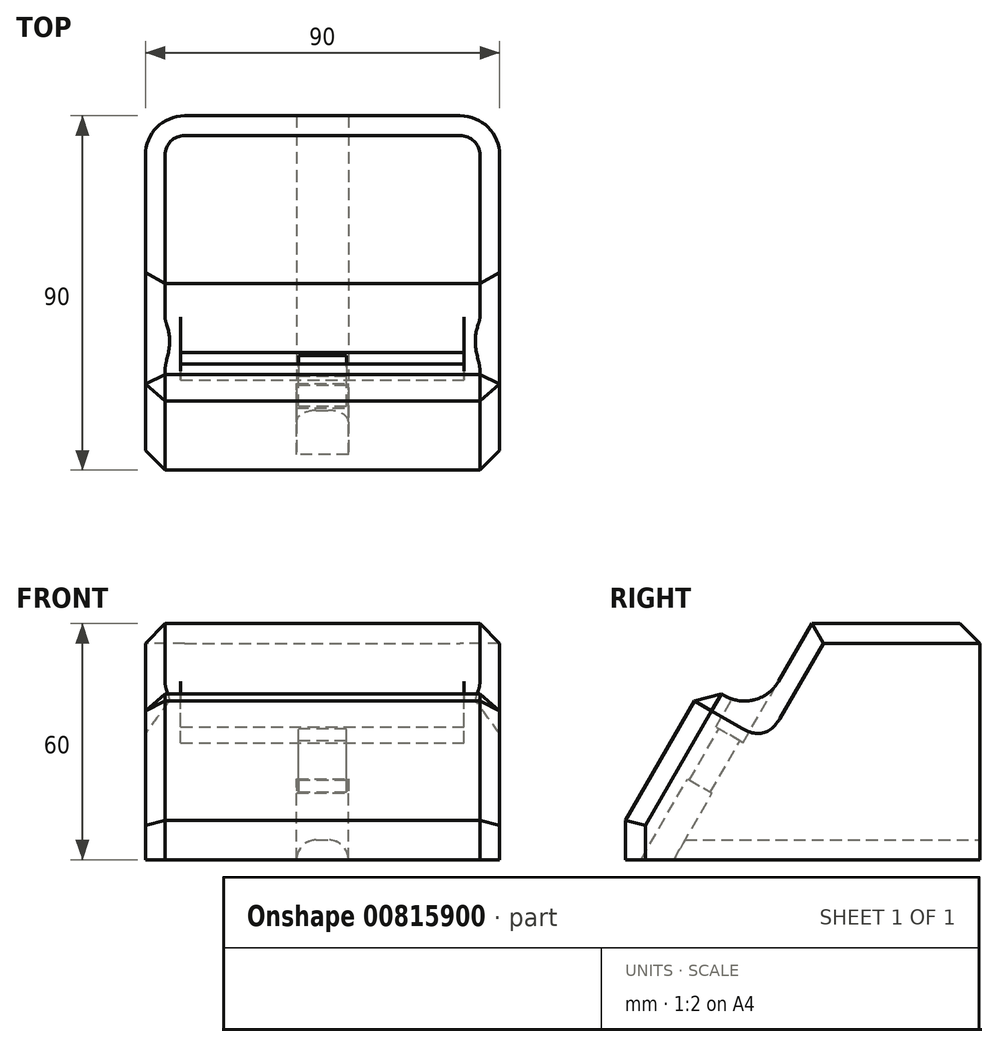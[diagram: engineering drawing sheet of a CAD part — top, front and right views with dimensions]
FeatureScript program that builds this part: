
annotation { "Feature Type Name" : "Feature", "Feature Type Description" : "" }
export const myFeature = defineFeature(function(context is Context, id is Id, definition is map)
    precondition{}
    {
        {
            var Q0;
            Q0=qCreatedBy(makeId("Top.planeOp"),FACE);
            var sketch = newSketch(context, id + "F0", { "sketchPlane" : qUnion([Q0])});
            skLineSegment(sketch, "E0.bottom", {"start": v(45, -45) * mm, "end": v(-45, -45) * mm});
            skLineSegment(sketch, "E0.top", {"start": v(35, 45) * mm, "end": v(-35, 45) * mm});
            skLineSegment(sketch, "E0.left", {"start": v(45, -45) * mm, "end": v(45, 35) * mm});
            skLineSegment(sketch, "E0.right", {"start": v(-45, -45) * mm, "end": v(-45, 35) * mm});
            skPoint(sketch, "E0.middle", {"position": v(0, 0) * mm});
            skPoint(sketch, "E1.visualSharp", {"position": v(-45, 45) * mm});
            skArc(sketch, "E1.filletArc", {"start": v(-35, 45) * mm, "mid": v(-42.07, 42.07) * mm, "end": v(-45, 35) * mm});
            skPoint(sketch, "E2.visualSharp", {"position": v(45, 45) * mm});
            skArc(sketch, "E2.filletArc", {"start": v(45, 35) * mm, "mid": v(42.07, 42.07) * mm, "end": v(35, 45) * mm});
            skSolve(sketch);
        }
        {
            var Q0;
            Q0=makeQuery(id+"F0.imprint","IMPRINT",FACE,{"disambiguationData":[TD([[makeQuery(id+"F0.imprint","IMPRINT",EDGE,{"derivedFrom":sQuery(id+"F0.wireOp",EDGE,"E0.bottom")}),-1.0]])]});
            extrude(context, id + "F1", {"entities" : qUnion([Q0]), "depth" : 60 * mm, "offsetDistance" : 25 * mm});
        }
        {
            var Q0;
            Q0=qCreatedBy(makeId("Right.planeOp"),FACE);
            var sketch = newSketch(context, id + "F2", { "sketchPlane" : qUnion([Q0])});
            skLineSegment(sketch, "E3", {"start": v(-45, 10) * mm, "end": v(-25, 44.64) * mm});
            skLineSegment(sketch, "E4", {"start": v(-45, 60) * mm, "end": v(2.34, 60) * mm});
            skLineSegment(sketch, "E5", {"start": v(-45, 60) * mm, "end": v(-45, 10) * mm});
            skLineSegment(sketch, "E6", {"start": v(-25, 44.64) * mm, "end": v(-11.14, 36.64) * mm});
            skLineSegment(sketch, "E7", {"start": v(-11.14, 36.64) * mm, "end": v(2.34, 60) * mm});
            skSolve(sketch);
        }
        {
            var Q0;
            Q0 = qSketchRegion(id + "F2", true);
            extrude(context, id + "F3", {"entities" : qUnion([Q0]), "operationType" : NewBodyOperationType.REMOVE, "endBound" : BoundingType.THROUGH_ALL, "oppositeDirection" : true, "depth" : 25 * mm, "offsetDistance" : 25 * mm, "hasSecondDirection" : true, "secondDirectionBound" : SecondDirectionBoundingType.THROUGH_ALL, "secondDirectionOppositeDirection" : false, "secondDirectionDepth" : 25 * mm});
        }
        {
            var Q0;
            Q0=makeQuery(id+"F3.boolean.opBoolean","COPY",FACE,{"derivedFrom":makeQuery(id+"F3.opExtrude","SWEPT_FACE",FACE,{"disambiguationData":[OSD([sQuery(id+"F2.wireOp",EDGE,"E6")])]})});
            var sketch = newSketch(context, id + "F4", { "sketchPlane" : qUnion([Q0])});
            skLineSegment(sketch, "E8.bottom", {"start": v(-36, -27.97) * mm, "end": v(36, -27.97) * mm});
            skLineSegment(sketch, "E8.top", {"start": v(-36, -35.97) * mm, "end": v(36, -35.97) * mm});
            skLineSegment(sketch, "E8.left", {"start": v(-36, -27.97) * mm, "end": v(-36, -35.97) * mm});
            skLineSegment(sketch, "E8.right", {"start": v(36, -27.97) * mm, "end": v(36, -35.97) * mm});
            skLineSegment(sketch, "E9", {"start": v(0, 0) * mm, "end": v(0, -27.97) * mm, "construction": true});
            skSolve(sketch);
        }
        {
            var Q0;
            Q0 = qSketchRegion(id + "F4", true);
            extrude(context, id + "F5", {"entities" : qUnion([Q0]), "operationType" : NewBodyOperationType.REMOVE, "oppositeDirection" : true, "depth" : 8 * mm, "offsetDistance" : 25 * mm});
        }
        {
            var Q0;
            Q0=makeQuery(id+"F3.boolean.opBoolean","INTERSECT",EDGE,{"derivedFrom":[makeQuery(id+"F1.opExtrude","SWEPT_FACE",FACE,{"disambiguationData":[OSD([sQuery(id+"F0.wireOp",EDGE,"E0.left")])]}),makeQuery(id+"F3.opExtrude","SWEPT_FACE",FACE,{"disambiguationData":[OSD([sQuery(id+"F2.wireOp",EDGE,"E3")])]})]});
            var Q1;
            Q1=makeQuery(id+"F3.boolean.opBoolean","INTERSECT",EDGE,{"derivedFrom":[makeQuery(id+"F1.opExtrude","SWEPT_FACE",FACE,{"disambiguationData":[OSD([sQuery(id+"F0.wireOp",EDGE,"E0.right")])]}),makeQuery(id+"F3.opExtrude","SWEPT_FACE",FACE,{"disambiguationData":[OSD([sQuery(id+"F2.wireOp",EDGE,"E3")])]})]});
            var Q2;
            Q2=makeQuery(id+"F1.opExtrude","SWEPT_EDGE",EDGE,{"disambiguationData":[OSD([sQuery(id+"F0.wireOp",EDGE,"E0.bottom"),sQuery(id+"F0.wireOp",EDGE,"E0.right")])]});
            var Q3;
            Q3=makeQuery(id+"F1.opExtrude","SWEPT_EDGE",EDGE,{"disambiguationData":[OSD([sQuery(id+"F0.wireOp",EDGE,"E0.bottom"),sQuery(id+"F0.wireOp",EDGE,"E0.left")])]});
            var Q4;
            Q4=makeQuery(id+"F3.boolean.opBoolean","INTERSECT",EDGE,{"derivedFrom":[makeQuery(id+"F1.opExtrude","SWEPT_FACE",FACE,{"disambiguationData":[OSD([sQuery(id+"F0.wireOp",EDGE,"E0.left")])]}),makeQuery(id+"F3.opExtrude","SWEPT_FACE",FACE,{"disambiguationData":[OSD([sQuery(id+"F2.wireOp",EDGE,"E7")])]})]});
            var Q5;
            Q5=makeQuery(id+"F3.boolean.opBoolean","INTERSECT",EDGE,{"derivedFrom":[makeQuery(id+"F1.opExtrude","SWEPT_FACE",FACE,{"disambiguationData":[OSD([sQuery(id+"F0.wireOp",EDGE,"E0.right")])]}),makeQuery(id+"F3.opExtrude","SWEPT_FACE",FACE,{"disambiguationData":[OSD([sQuery(id+"F2.wireOp",EDGE,"E7")])]})]});
            var Q6;
            Q6=makeQuery(id+"F3.boolean.opBoolean","COPY",EDGE,{"derivedFrom":makeQuery(id+"F3.opExtrude","SWEPT_EDGE",EDGE,{"disambiguationData":[OSD([sQuery(id+"F2.wireOp",EDGE,"E3"),sQuery(id+"F2.wireOp",EDGE,"E6")])]})});
            var Q7;
            Q7=makeQuery(id+"F3.boolean.opBoolean","INTERSECT",EDGE,{"derivedFrom":[makeQuery(id+"F1.opExtrude","SWEPT_FACE",FACE,{"disambiguationData":[OSD([sQuery(id+"F0.wireOp",EDGE,"E0.left")])]}),makeQuery(id+"F3.opExtrude","SWEPT_FACE",FACE,{"disambiguationData":[OSD([sQuery(id+"F2.wireOp",EDGE,"E6")])]})]});
            var Q8;
            Q8=makeQuery(id+"F3.boolean.opBoolean","INTERSECT",EDGE,{"derivedFrom":[makeQuery(id+"F1.opExtrude","SWEPT_FACE",FACE,{"disambiguationData":[OSD([sQuery(id+"F0.wireOp",EDGE,"E0.right")])]}),makeQuery(id+"F3.opExtrude","SWEPT_FACE",FACE,{"disambiguationData":[OSD([sQuery(id+"F2.wireOp",EDGE,"E6")])]})]});
            var Q9;
            Q9=makeQuery(id+"F1.opExtrude","CAP_EDGE",EDGE,{"disambiguationData":[OSD([sQuery(id+"F0.wireOp",EDGE,"E0.top")])],"isStart":false});
            chamfer(context, id + "F6", {"entities" : qUnion([Q0, Q1, Q2, Q3, Q4, Q5, Q6, Q7, Q8, Q9]), "width" : 5 * mm, "tangentPropagation" : true});
        }
        {
            var Q0;
            {var subQ0=makeQuery(id+"F1.opExtrude","SWEPT_FACE",FACE,{"disambiguationData":[OSD([sQuery(id+"F0.wireOp",EDGE,"E0.right")])]});Q0=makeQuery(id+"F6.opChamfer","BLEND_EDGE",EDGE,{"blendedFrom":[makeQuery(id+"F3.boolean.opBoolean","INTERSECT",EDGE,{"derivedFrom":[subQ0,makeQuery(id+"F3.opExtrude","SWEPT_FACE",FACE,{"disambiguationData":[OSD([sQuery(id+"F2.wireOp",EDGE,"E6")])]})]}),makeQuery(id+"F3.boolean.opBoolean","INTERSECT",EDGE,{"derivedFrom":[subQ0,makeQuery(id+"F3.opExtrude","SWEPT_FACE",FACE,{"disambiguationData":[OSD([sQuery(id+"F2.wireOp",EDGE,"E7")])]})]})],"blendedInto":[]});}
            var Q1;
            {var subQ0=makeQuery(id+"F1.opExtrude","SWEPT_FACE",FACE,{"disambiguationData":[OSD([sQuery(id+"F0.wireOp",EDGE,"E0.left")])]});Q1=makeQuery(id+"F6.opChamfer","BLEND_EDGE",EDGE,{"blendedFrom":[makeQuery(id+"F3.boolean.opBoolean","INTERSECT",EDGE,{"derivedFrom":[subQ0,makeQuery(id+"F3.opExtrude","SWEPT_FACE",FACE,{"disambiguationData":[OSD([sQuery(id+"F2.wireOp",EDGE,"E6")])]})]}),makeQuery(id+"F3.boolean.opBoolean","INTERSECT",EDGE,{"derivedFrom":[subQ0,makeQuery(id+"F3.opExtrude","SWEPT_FACE",FACE,{"disambiguationData":[OSD([sQuery(id+"F2.wireOp",EDGE,"E7")])]})]})],"blendedInto":[]});}
            fillet(context, id + "F7", {"entities" : qUnion([Q0, Q1]), "radius" : 10 * mm, "rho" : 0.5, "crossSection" : FilletCrossSection.CONIC, "allowEdgeOverflow" : false});
        }
        {
            var Q0;
            {var subQ0=sQuery(id+"F2.wireOp",EDGE,"E6");var subQ1=sQuery(id+"F2.wireOp",EDGE,"E7");Q0=makeQuery(id+"F5.boolean.opBoolean","SPLIT",EDGE,{"disambiguationData":[TD([makeQuery(id+"F1.opExtrude","SWEPT_FACE",FACE,{"disambiguationData":[OSD([sQuery(id+"F0.wireOp",EDGE,"E0.right")])]})])],"derivedFrom":makeQuery(id+"F3.boolean.opBoolean","COPY",EDGE,{"derivedFrom":makeQuery(id+"F3.opExtrude","SWEPT_EDGE",EDGE,{"disambiguationData":[OSD([subQ0,subQ1])]})})});}
            var Q1;
            {var subQ0=sQuery(id+"F2.wireOp",EDGE,"E6");var subQ1=sQuery(id+"F2.wireOp",EDGE,"E7");Q1=makeQuery(id+"F5.boolean.opBoolean","SPLIT",EDGE,{"disambiguationData":[TD([makeQuery(id+"F1.opExtrude","SWEPT_FACE",FACE,{"disambiguationData":[OSD([sQuery(id+"F0.wireOp",EDGE,"E0.left")])]})])],"derivedFrom":makeQuery(id+"F3.boolean.opBoolean","COPY",EDGE,{"derivedFrom":makeQuery(id+"F3.opExtrude","SWEPT_EDGE",EDGE,{"disambiguationData":[OSD([subQ0,subQ1])]})})});}
            fillet(context, id + "F8", {"entities" : qUnion([Q0, Q1]), "radius" : 10 * mm, "tangentPropagation" : true, "allowEdgeOverflow" : false});
        }
        {
            var Q0;
            Q0=makeQuery(id+"F5.boolean.opBoolean","COPY",FACE,{"derivedFrom":makeQuery(id+"F5.opExtrude","CAP_FACE",FACE,{"disambiguationData":[OSD([sQuery(id+"F4.wireOp",EDGE,"E8.bottom"),sQuery(id+"F4.wireOp",EDGE,"E8.top"),sQuery(id+"F4.wireOp",EDGE,"E8.left"),sQuery(id+"F4.wireOp",EDGE,"E8.right")])],"isStart":false})});
            var sketch = newSketch(context, id + "F9", { "sketchPlane" : qUnion([Q0])});
            skLineSegment(sketch, "E10.bottom", {"start": v(6.1, -28.87) * mm, "end": v(-6.1, -28.87) * mm});
            skLineSegment(sketch, "E10.top", {"start": v(6.1, -35.07) * mm, "end": v(-6.1, -35.07) * mm});
            skLineSegment(sketch, "E10.left", {"start": v(6.1, -28.87) * mm, "end": v(6.1, -35.07) * mm});
            skLineSegment(sketch, "E10.right", {"start": v(-6.1, -28.87) * mm, "end": v(-6.1, -35.07) * mm});
            skPoint(sketch, "E10.middle", {"position": v(0, -31.97) * mm});
            skLineSegment(sketch, "E11", {"start": v(0, -31.97) * mm, "end": v(0, 0) * mm, "construction": true});
            skLineSegment(sketch, "E12", {"start": v(-6.1, -35.07) * mm, "end": v(-6.1, -35.97) * mm, "construction": true});
            skLineSegment(sketch, "E13", {"start": v(-6.1, -28.87) * mm, "end": v(-6.1, -27.97) * mm, "construction": true});
            skSolve(sketch);
        }
        {
            var Q0;
            Q0 = qSketchRegion(id + "F9", true);
            extrude(context, id + "F10", {"entities" : qUnion([Q0]), "operationType" : NewBodyOperationType.REMOVE, "oppositeDirection" : true, "depth" : 21 * mm, "offsetDistance" : 25 * mm});
        }
        {
            var Q0;
            Q0=makeQuery(id+"F10.boolean.opBoolean","COPY",FACE,{"derivedFrom":makeQuery(id+"F10.opExtrude","CAP_FACE",FACE,{"disambiguationData":[OSD([sQuery(id+"F9.wireOp",EDGE,"E10.bottom"),sQuery(id+"F9.wireOp",EDGE,"E10.top"),sQuery(id+"F9.wireOp",EDGE,"E10.left"),sQuery(id+"F9.wireOp",EDGE,"E10.right")])],"isStart":false})});
            var sketch = newSketch(context, id + "F11", { "sketchPlane" : qUnion([Q0])});
            skLineSegment(sketch, "E14.bottom", {"start": v(-6.6, -35.57) * mm, "end": v(6.6, -35.57) * mm});
            skLineSegment(sketch, "E14.top", {"start": v(-6.6, -28.37) * mm, "end": v(6.6, -28.37) * mm});
            skLineSegment(sketch, "E14.left", {"start": v(-6.6, -35.57) * mm, "end": v(-6.6, -28.37) * mm});
            skLineSegment(sketch, "E14.right", {"start": v(6.6, -35.57) * mm, "end": v(6.6, -28.37) * mm});
            skPoint(sketch, "E14.middle", {"position": v(0, -31.97) * mm});
            skSolve(sketch);
        }
        {
            var Q0;
            Q0 = qSketchRegion(id + "F11", true);
            extrude(context, id + "F12", {"entities" : qUnion([Q0]), "operationType" : NewBodyOperationType.REMOVE, "endBound" : BoundingType.UP_TO_NEXT, "oppositeDirection" : true, "depth" : 25 * mm, "offsetDistance" : 25 * mm});
        }
        {
            var Q0;
            Q0 = qSketchRegion(id + "F11", true);
            extrude(context, id + "F13", {"entities" : qUnion([Q0]), "operationType" : NewBodyOperationType.REMOVE, "depth" : 6 * mm, "offsetDistance" : 25 * mm});
        }
        {
            var Q0;
            Q0=makeQuery(id+"F1.opExtrude","CAP_FACE",FACE,{"disambiguationData":[OSD([sQuery(id+"F0.wireOp",EDGE,"E0.bottom"),sQuery(id+"F0.wireOp",EDGE,"E0.top"),sQuery(id+"F0.wireOp",EDGE,"E0.left"),sQuery(id+"F0.wireOp",EDGE,"E0.right"),sQuery(id+"F0.wireOp",EDGE,"E1.filletArc"),sQuery(id+"F0.wireOp",EDGE,"E2.filletArc")])],"isStart":true});
            var sketch = newSketch(context, id + "F14", { "sketchPlane" : qUnion([Q0])});
            skLineSegment(sketch, "E15.bottom", {"start": v(-6.6, 32.76) * mm, "end": v(6.6, 32.76) * mm});
            skLineSegment(sketch, "E15.top", {"start": v(-6.6, -45) * mm, "end": v(6.6, -45) * mm});
            skLineSegment(sketch, "E15.left", {"start": v(-6.6, 32.76) * mm, "end": v(-6.6, -45) * mm});
            skLineSegment(sketch, "E15.right", {"start": v(6.6, 32.76) * mm, "end": v(6.6, -45) * mm});
            skSolve(sketch);
        }
        {
            var Q0;
            Q0 = qSketchRegion(id + "F14", true);
            extrude(context, id + "F15", {"entities" : qUnion([Q0]), "operationType" : NewBodyOperationType.REMOVE, "oppositeDirection" : true, "depth" : 5 * mm, "offsetDistance" : 25 * mm});
        }
        {
            var Q0;
            Q0=makeQuery(id+"F15.boolean.opBoolean","COPY",EDGE,{"derivedFrom":makeQuery(id+"F15.opExtrude","CAP_EDGE",EDGE,{"disambiguationData":[OSD([sQuery(id+"F14.wireOp",EDGE,"E15.right")])],"isStart":false})});
            var Q1;
            Q1=makeQuery(id+"F15.boolean.opBoolean","COPY",EDGE,{"derivedFrom":makeQuery(id+"F15.opExtrude","CAP_EDGE",EDGE,{"disambiguationData":[OSD([sQuery(id+"F14.wireOp",EDGE,"E15.left")])],"isStart":false})});
            fillet(context, id + "F16", {"entities" : qUnion([Q0, Q1]), "radius" : 5 * mm, "tangentPropagation" : true, "allowEdgeOverflow" : false});
        }
    });
